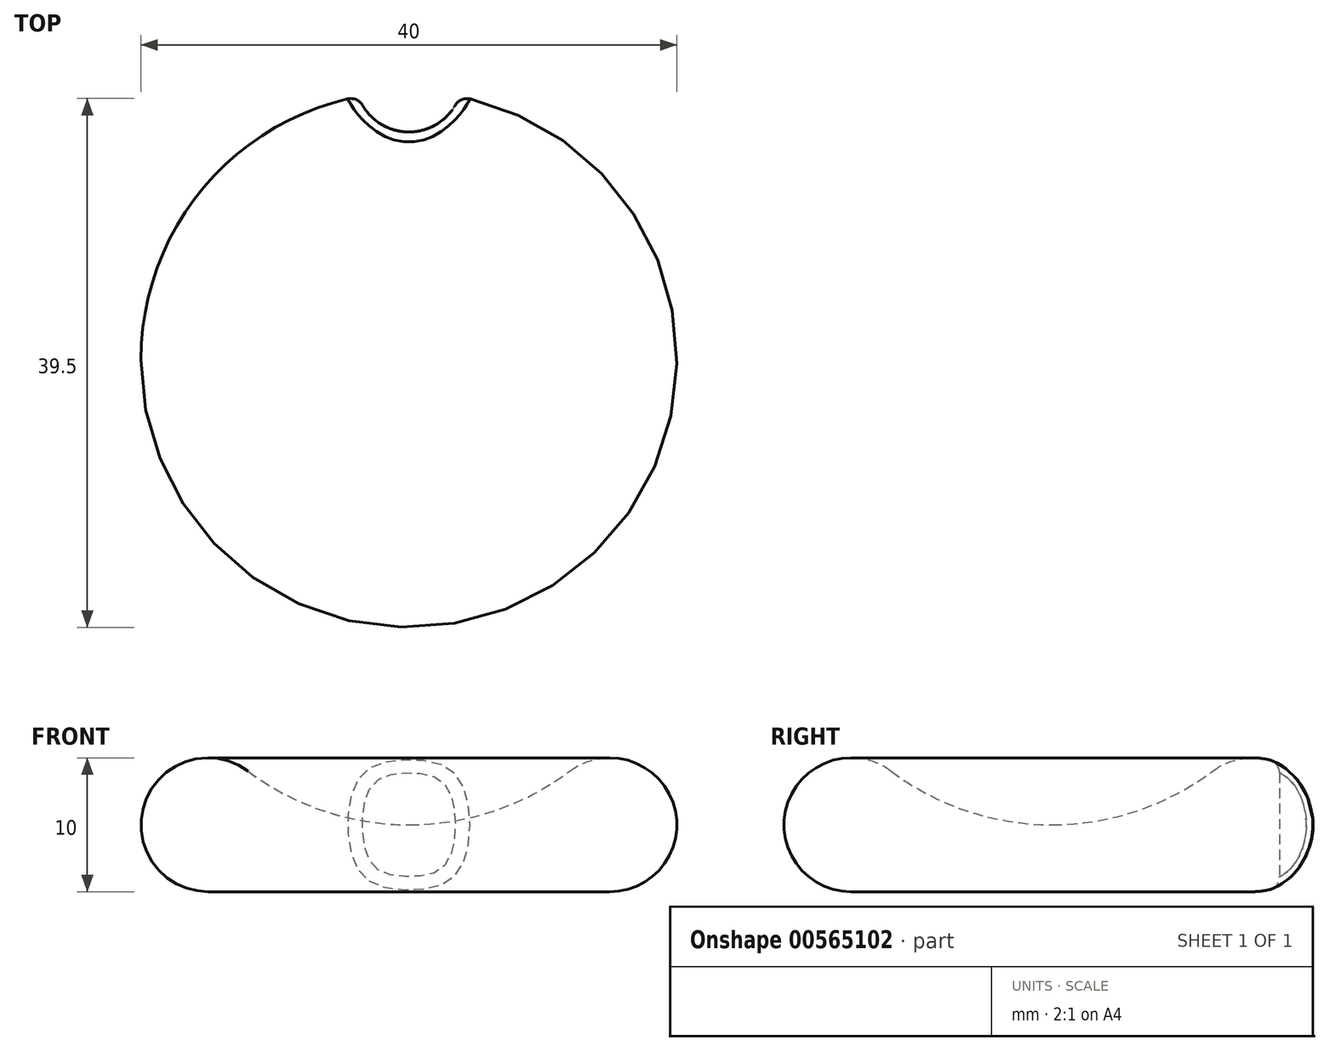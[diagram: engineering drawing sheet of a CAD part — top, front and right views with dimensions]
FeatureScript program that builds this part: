
annotation { "Feature Type Name" : "Feature", "Feature Type Description" : "" }
export const myFeature = defineFeature(function(context is Context, id is Id, definition is map)
    precondition{}
    {
        {
            var Q0;
            Q0=qCreatedBy(makeId("Front.planeOp"),FACE);
            var sketch = newSketch(context, id + "F0", { "sketchPlane" : qUnion([Q0])});
            skArc(sketch, "E0", {"start": v(-12, 9) * mm, "mid": v(-19.74, 6.58) * mm, "end": v(-15, 0) * mm});
            skArc(sketch, "E1", {"start": v(-12, 9) * mm, "mid": v(-6.32, 6.03) * mm, "end": v(0, 5) * mm});
            skLineSegment(sketch, "E2", {"start": v(-15, 0) * mm, "end": v(0, 0) * mm});
            skLineSegment(sketch, "E3", {"start": v(0, 0) * mm, "end": v(0, 5) * mm});
            skSolve(sketch);
        }
        {
            var Q0;
            Q0=makeQuery(id+"F0.imprint","IMPRINT",FACE,{"disambiguationData":[TD([[makeQuery(id+"F0.imprint","IMPRINT",EDGE,{"derivedFrom":sQuery(id+"F0.wireOp",EDGE,"E0")}),1.0]])]});
            var Q1;
            Q1=sQuery(id+"F0.wireOp",EDGE,"E3");
            revolve(context, id + "F1", {"entities" : qUnion([Q0]), "axis" : qUnion([Q1]), "revolveType" : RevolveType.FULL});
        }
        {
            var Q0;
            Q0=qCreatedBy(makeId("Top.planeOp"),FACE);
            var sketch = newSketch(context, id + "F2", { "sketchPlane" : qUnion([Q0])});
            skCircle(sketch, "E4", {"center": v(0, 21) * mm, "radius": 4 * mm});
            skSolve(sketch);
        }
        {
            var Q0;
            Q0 = qSketchRegion(id + "F2", true);
            extrude(context, id + "F3", {"entities" : qUnion([Q0]), "operationType" : NewBodyOperationType.REMOVE, "depth" : 25.4 * mm, "offsetDistance" : 25.4 * mm});
        }
        {
            var Q0;
            Q0=makeQuery(id+"F3.boolean.opBoolean","COPY",FACE,{"derivedFrom":makeQuery(id+"F3.opExtrude","SWEPT_FACE",FACE,{"disambiguationData":[OSD([sQuery(id+"F2.wireOp",EDGE,"E4")])]})});
            fillet(context, id + "F4", {"entities" : qUnion([Q0]), "radius" : 1 * mm, "tangentPropagation" : true, "allowEdgeOverflow" : false});
        }
    });
